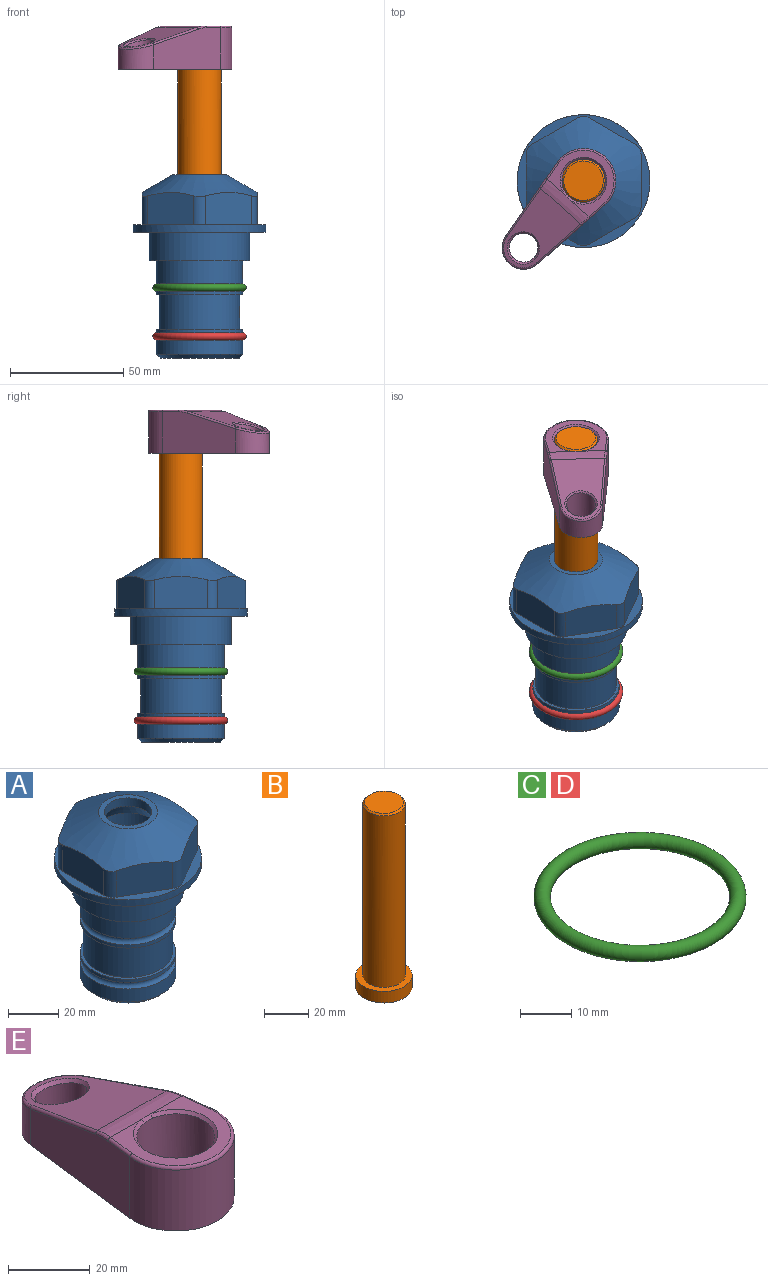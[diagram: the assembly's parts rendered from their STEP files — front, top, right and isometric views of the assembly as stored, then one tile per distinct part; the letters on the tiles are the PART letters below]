
ASSEMBLY  parts=5 mates=4
PART A: 36 faces, bbox 58.7x58.7x81 mm
  f0: cylinder r=17.78mm len=35.56mm, axis (0,0,1), area 1670.8mm2, adj f23,f24,f31
  f1: cylinder r=19.05mm len=38.1mm, axis (0,0,1), area 1191.9mm2, adj f26,f27,f30
  f2: plane 58.66x58.66mm, normal (0,0,-1), area 1150.6mm2, adj f3,f28
  f3: cylinder r=29.33mm len=58.66mm, axis (0,0,-1), area 585.1mm2, adj f2,f4
  f4: plane 58.66x58.66mm, normal (0,0,1), area 475.9mm2, adj f3,f5,f6,f7,f8,f9,f10,f11
  f5: plane 20.32x14.34mm, normal (-0.5,0.87,0), area 324.4mm2, adj f4,f15,f16,f17
  f6: plane 20.32x14.34mm, normal (0.5,0.87,0), area 324.4mm2, adj f4,f14,f15,f17
  f7: plane 23.48x14.34mm, normal (1,0,0), area 324.4mm2, adj f4,f13,f14,f17
  f8: plane 20.32x14.34mm, normal (0.5,-0.87,0), area 324.4mm2, adj f4,f12,f13,f17
  f9: plane 20.32x14.34mm, normal (-0.5,-0.87,0), area 324.4mm2, adj f4,f11,f12,f17
  f10: plane 23.48x14.34mm, normal (-1,0,0), area 324.4mm2, adj f4,f11,f16,f17
  f11: cylinder r=5.08mm len=12.85mm, axis (0,0,-1), area 67.2mm2, adj f4,f9,f10,f17
  f12: cylinder r=5.08mm len=12.85mm, axis (0,0,-1), area 67.2mm2, adj f4,f8,f9,f17
  f13: cylinder r=5.08mm len=12.85mm, axis (0,0,-1), area 67.2mm2, adj f4,f7,f8,f17
  f14: cylinder r=5.08mm len=12.85mm, axis (0,0,-1), area 67.2mm2, adj f4,f6,f7,f17
  f15: cylinder r=5.08mm len=12.85mm, axis (0,0,-1), area 67.2mm2, adj f4,f5,f6,f17
  f16: cylinder r=5.08mm len=12.85mm, axis (0,0,-1), area 67.2mm2, adj f4,f5,f10,f17
  f17: cone r=11.73mm half-angle=60deg, axis (0,0,-1), area 2071.8mm2, adj f5,f6,f7,f8,f9,f10,f11,f12
  f18: plane 23.46x23.46mm, normal (0,0,1), area 147.4mm2, adj f17,f35
  f19: plane 34.93x34.93mm, normal (0,0,-1), area 958mm2, adj f29
  f20: cylinder r=19.05mm len=38.1mm, axis (0,0,1), area 760.1mm2, adj f21,f29
  f21: torus R=19.05mm, axis (0,0,1), area 565.3mm2, adj f20,f22
  f22: cylinder r=19.05mm len=38.1mm, axis (0,0,1), area 190mm2, adj f21,f23
  f23: plane 38.1x38.1mm, normal (0,0,1), area 146.9mm2, adj f0,f22
  f24: plane 38.1x38.1mm, normal (0,0,-1), area 146.9mm2, adj f0,f25
  f25: cylinder r=19.05mm len=38.1mm, axis (0,0,1), area 190mm2, adj f24,f26
  f26: torus R=19.05mm, axis (0,0,1), area 565.3mm2, adj f1,f25
  f27: plane 44.45x44.45mm, normal (0,0,-1), area 411.7mm2, adj f1,f28
  f28: cylinder r=22.23mm len=44.45mm, axis (0,0,1), area 1773.5mm2, adj f2,f27
  f29: cone r=19.05mm half-angle=45deg, axis (0,0,1), area 257.5mm2, adj f19,f20
  f30: cylinder r=3.17mm len=6.75mm, axis (-1,0,0), area 128mm2, adj f1,f33
  f31: cylinder r=3.17mm len=6.35mm, axis (-1,0,0), area 102.5mm2, adj f0,f33
  f32: plane 25.4x25.4mm, normal (0,0,1), area 506.7mm2, adj f33
  f33: cylinder r=12.7mm len=66.42mm, axis (0,0,-1), area 5236.2mm2, adj f30,f31,f32,f34
  f34: cone r=9.53mm half-angle=30deg, axis (0,0,-1), area 443.4mm2, adj f33,f35
  f35: cylinder r=9.53mm len=19.05mm, axis (0,0,-1), area 240.9mm2, adj f18,f34
PART B: 6 faces, bbox 25.4x25.4x101.6 mm
  f0: plane 17.46x17.46mm, normal (0,0,1), area 239.5mm2, adj f5
  f1: plane 25.4x25.4mm, normal (0,0,-1), area 506.7mm2, adj f2
  f2: cylinder r=12.7mm len=25.4mm, axis (0,0,1), area 506.7mm2, adj f1,f3
  f3: plane 25.4x25.4mm, normal (0,0,1), area 221.7mm2, adj f2,f4
  f4: cylinder r=9.53mm len=94.46mm, axis (0,0,1), area 5653mm2, adj f3,f5
  f5: cone r=8.73mm half-angle=45deg, axis (0,0,-1), area 64.4mm2, adj f0,f4
PART C: 1 faces, bbox 44.7x44.7x3.2 mm
  f0: torus R=19.05mm, axis (0,0,1), area 1193.9mm2
PART D: same geometry as C
PART E: 31 faces, bbox 31.7x65.5x19.8 mm
  f0: plane 39.12x18.26mm, normal (0.99,0.12,0), area 612.2mm2, adj f1,f4,f7,f11,f13,f15
  f1: cylinder r=9.53mm len=18.91mm, axis (0,0,-1), area 296.1mm2, adj f0,f2,f7,f17
  f2: plane 39.12x18.26mm, normal (-0.99,0.12,0), area 612.2mm2, adj f1,f4,f7,f12,f14,f16
  f3: cylinder r=6.35mm len=12.7mm, axis (0,0,-1), area 362.4mm2, adj f7,f18
  f4: cylinder r=14.29mm len=28.58mm, axis (0,0,-1), area 882.2mm2, adj f0,f2,f7,f10
  f5: cylinder r=9.53mm len=19.05mm, axis (0,0,-1), area 1092.6mm2, adj f7,f19,f20
  f6: plane 26.99x23.69mm, normal (0,0,1), area 216.2mm2, adj f9,f10,f11,f12,f19
  f7: plane 63.5x28.58mm, normal (0,0,-1), area 661.8mm2, adj f0,f1,f2,f3,f4,f5,f22,f23
  f8: plane 33.52x23.6mm, normal (0,0.26,0.97), area 486mm2, adj f9,f15,f16,f17,f18
  f9: cylinder r=19.05mm len=24.72mm, axis (1,0,0), area 120.4mm2, adj f6,f8,f13,f14,f20
  f10: torus R=13.49mm, axis (0,0,1), area 59mm2, adj f4,f6,f11,f12
  f11: cylinder r=0.79mm len=8.67mm, axis (0.12,-0.99,0), area 10.8mm2, adj f0,f6,f10,f13
  f12: cylinder r=0.79mm len=8.67mm, axis (0.12,0.99,0), area 10.8mm2, adj f2,f6,f10,f14
  f13: bspline ~4.95x1.42mm, area 6.1mm2, adj f0,f9,f11,f15
  f14: bspline ~4.95x1.42mm, area 6.1mm2, adj f2,f9,f12,f16
  f15: cylinder r=0.79mm len=25.95mm, axis (0.12,-0.96,0.26), area 32.9mm2, adj f0,f8,f13,f17
  f16: cylinder r=0.79mm len=25.95mm, axis (0.12,0.96,-0.26), area 32.9mm2, adj f2,f8,f14,f17
  f17: bspline ~18.91x8.38mm, area 30mm2, adj f1,f8,f15,f16
  f18: bspline ~14.29x14.29mm, area 48.3mm2, adj f3,f8
  f19: cone r=9.53mm half-angle=45deg, axis (0,0,1), area 66.5mm2, adj f5,f6,f20
  f20: bspline ~3.22x0.96mm, area 3.5mm2, adj f5,f9,f19
  f21: plane 2.75x2.72mm, normal (0,0,-1), area 2.9mm2, adj f23,f25,f28
  f22: plane 23.05x15.88mm, normal (-0.99,-0.12,0), area 323.6mm2, adj f7,f25,f26,f27,f28,f29
  f23: plane 23.05x15.88mm, normal (0.99,-0.12,0), area 323.6mm2, adj f7,f21,f25,f27,f28,f30
  f24: cylinder r=9.53mm len=10.69mm, axis (0,0,-1), area 114.7mm2, adj f7,f27,f29,f30
  f25: cylinder r=12.7mm len=20.59mm, axis (0,0,-1), area 381.1mm2, adj f7,f21,f22,f23,f26,f28
  f26: plane 2.75x2.72mm, normal (0,0,-1), area 2.9mm2, adj f22,f25,f28
  f27: plane 19.72x18.37mm, normal (0,-0.26,-0.97), area 291.8mm2, adj f22,f23,f24,f28,f29,f30
  f28: cylinder r=15.88mm len=19.92mm, axis (1,0,0), area 54.8mm2, adj f21,f22,f23,f25,f26,f27
  f29: cylinder r=1.59mm len=11mm, axis (0,0,-1), area 34.7mm2, adj f7,f22,f24,f27
  f30: cylinder r=1.59mm len=11mm, axis (0,0,-1), area 34.7mm2, adj f7,f23,f24,f27
PLACE A at identity fixed
PLACE B rot(axis=(0,0,1),138.2deg) t=(0,0,27.55)mm
PLACE C at identity
PLACE D t=(0,0,-21.59)mm
PLACE E rot(axis=(0,0,1),138.2deg) t=(0,0,27.55)mm
MATE fastened B.f2 <-> E.f4  axis (0,0,-1) through (0,0,90.26)mm
MATE cylindrical B.f2 <-> A.f0  axis (0,0,-1) through (0,0,-10.55)mm
MATE fastened D.f0 <-> A.f0  axis (0,0,1) through (0,0,-46.1)mm
MATE fastened C.f0 <-> A.f0  axis (0,0,1) through (0,0,-24.51)mm
